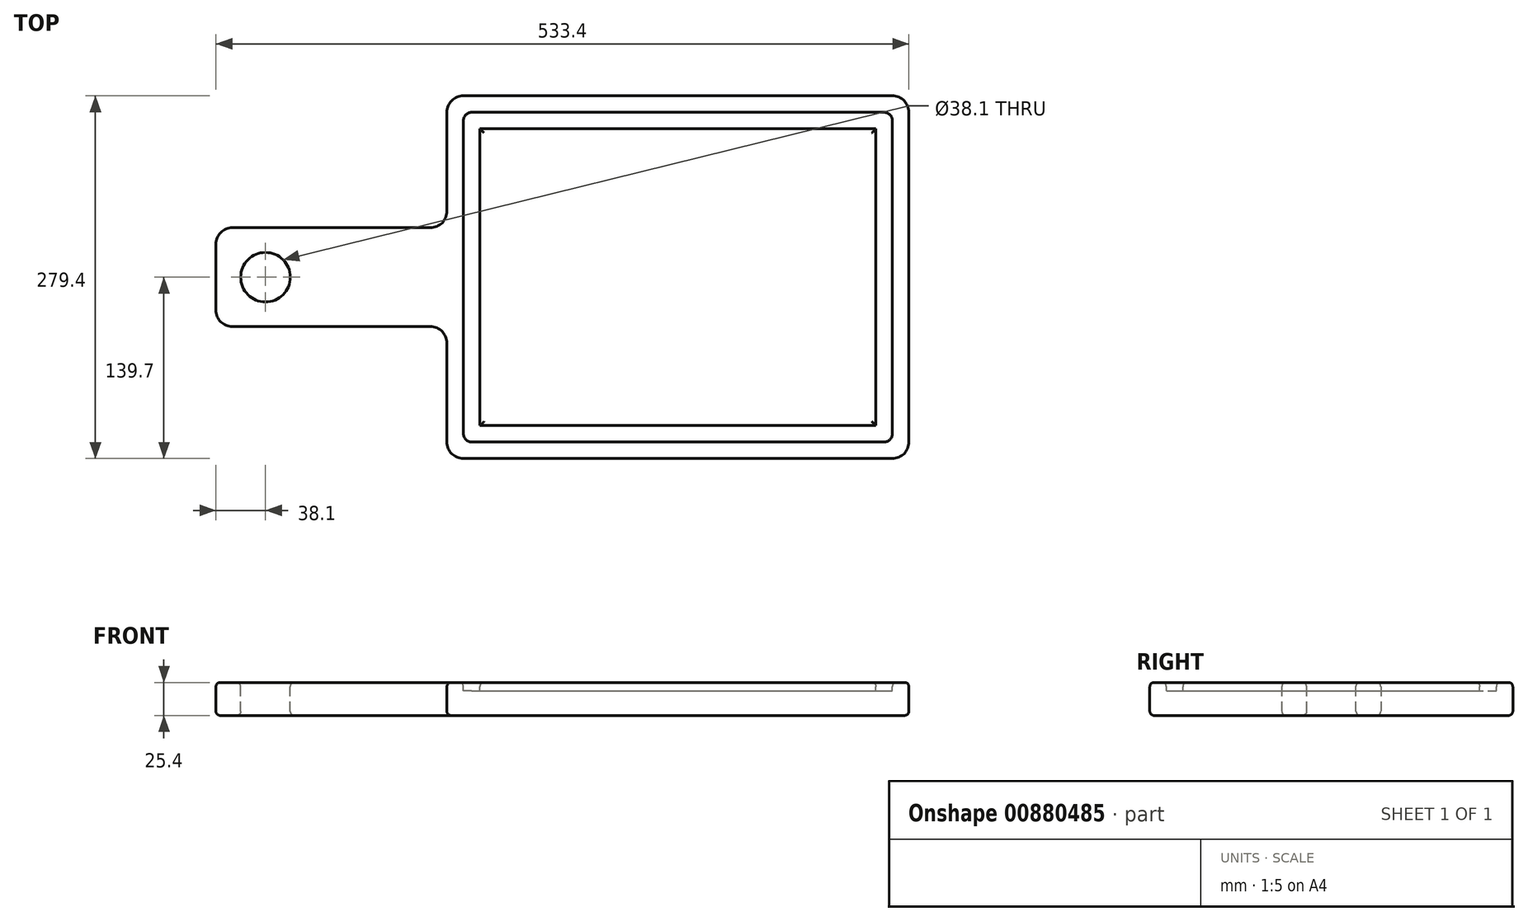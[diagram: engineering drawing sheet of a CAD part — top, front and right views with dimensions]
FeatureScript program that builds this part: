
annotation { "Feature Type Name" : "Feature", "Feature Type Description" : "" }
export const myFeature = defineFeature(function(context is Context, id is Id, definition is map)
    precondition{}
    {
        {
            var Q0;
            Q0=qCreatedBy(makeId("Top.planeOp"),FACE);
            var sketch = newSketch(context, id + "F0", { "sketchPlane" : qUnion([Q0])});
            skLineSegment(sketch, "E0.bottom", {"start": v(0, 0) * mm, "end": v(355.6, 0) * mm});
            skLineSegment(sketch, "E0.top", {"start": v(0, 279.4) * mm, "end": v(355.6, 279.4) * mm});
            skLineSegment(sketch, "E0.left", {"start": v(0, 0) * mm, "end": v(0, 279.4) * mm});
            skLineSegment(sketch, "E0.right", {"start": v(355.6, 0) * mm, "end": v(355.6, 279.4) * mm});
            skLineSegment(sketch, "E1.bottom", {"start": v(0, 177.8) * mm, "end": v(-177.8, 177.8) * mm});
            skLineSegment(sketch, "E1.top", {"start": v(0, 101.6) * mm, "end": v(-177.8, 101.6) * mm});
            skLineSegment(sketch, "E1.left", {"start": v(0, 177.8) * mm, "end": v(0, 101.6) * mm});
            skLineSegment(sketch, "E1.right", {"start": v(-177.8, 177.8) * mm, "end": v(-177.8, 101.6) * mm});
            skSolve(sketch);
        }
        {
            var Q0;
            {var subQ3=sQuery(id+"F0.wireOp",EDGE,"E0.bottom");Q0=makeQuery(id+"F0.imprint","IMPRINT",FACE,{"disambiguationData":[TD([[makeQuery(id+"F0.imprint","IMPRINT",EDGE,{"derivedFrom":subQ3}),1.0]])]});}
            var Q1;
            Q1=makeQuery(id+"F0.imprint","IMPRINT",FACE,{"disambiguationData":[TD([[makeQuery(id+"F0.imprint","IMPRINT",EDGE,{"derivedFrom":sQuery(id+"F0.wireOp",EDGE,"E1.bottom")}),1.0]])]});
            extrude(context, id + "F1", {"entities" : qUnion([Q0, Q1]), "depth" : 25.4 * mm, "offsetDistance" : 25.4 * mm});
        }
        {
            var Q0;
            Q0=makeQuery(id+"F1.opExtrude","CAP_FACE",FACE,{"disambiguationData":[OSD([sQuery(id+"F0.wireOp",EDGE,"E0.bottom"),sQuery(id+"F0.wireOp",EDGE,"E0.top"),sQuery(id+"F0.wireOp",EDGE,"E0.left"),sQuery(id+"F0.wireOp",EDGE,"E0.right"),sQuery(id+"F0.wireOp",EDGE,"E1.bottom"),sQuery(id+"F0.wireOp",EDGE,"E1.top"),sQuery(id+"F0.wireOp",EDGE,"E1.right")])],"isStart":false});
            var sketch = newSketch(context, id + "F2", { "sketchPlane" : qUnion([Q0])});
            skCircle(sketch, "E2", {"center": v(-139.7, 139.7) * mm, "radius": 19.05 * mm});
            skSolve(sketch);
        }
        {
            var Q0;
            Q0 = qSketchRegion(id + "F2", true);
            extrude(context, id + "F3", {"entities" : qUnion([Q0]), "operationType" : NewBodyOperationType.REMOVE, "oppositeDirection" : true, "depth" : 25.4 * mm, "offsetDistance" : 25.4 * mm});
        }
        {
            var Q0;
            Q0=makeQuery(id+"F1.opExtrude","CAP_FACE",FACE,{"disambiguationData":[OSD([sQuery(id+"F0.wireOp",EDGE,"E0.bottom"),sQuery(id+"F0.wireOp",EDGE,"E0.top"),sQuery(id+"F0.wireOp",EDGE,"E0.left"),sQuery(id+"F0.wireOp",EDGE,"E0.right"),sQuery(id+"F0.wireOp",EDGE,"E1.bottom"),sQuery(id+"F0.wireOp",EDGE,"E1.top"),sQuery(id+"F0.wireOp",EDGE,"E1.right")])],"isStart":false});
            var sketch = newSketch(context, id + "F4", { "sketchPlane" : qUnion([Q0])});
            skLineSegment(sketch, "E3.0", {"start": v(12.7, 12.7) * mm, "end": v(12.7, 101.6) * mm});
            skLineSegment(sketch, "E3.1", {"start": v(12.7, 177.8) * mm, "end": v(12.7, 266.7) * mm});
            skLineSegment(sketch, "E3.2", {"start": v(12.7, 266.7) * mm, "end": v(342.9, 266.7) * mm});
            skLineSegment(sketch, "E3.3", {"start": v(342.9, 12.7) * mm, "end": v(342.9, 266.7) * mm});
            skLineSegment(sketch, "E3.4", {"start": v(12.7, 12.7) * mm, "end": v(342.9, 12.7) * mm});
            skLineSegment(sketch, "E4", {"start": v(12.7, 177.8) * mm, "end": v(12.7, 101.6) * mm});
            skLineSegment(sketch, "E5.0", {"start": v(25.4, 177.8) * mm, "end": v(25.4, 254) * mm});
            skLineSegment(sketch, "E5.1", {"start": v(330.2, 25.4) * mm, "end": v(330.2, 254) * mm});
            skLineSegment(sketch, "E5.2", {"start": v(25.4, 25.4) * mm, "end": v(330.2, 25.4) * mm});
            skLineSegment(sketch, "E5.3", {"start": v(25.4, 254) * mm, "end": v(330.2, 254) * mm});
            skLineSegment(sketch, "E5.4", {"start": v(25.4, 25.4) * mm, "end": v(25.4, 101.6) * mm});
            skLineSegment(sketch, "E5.5", {"start": v(25.4, 177.8) * mm, "end": v(25.4, 101.6) * mm});
            skSolve(sketch);
        }
        {
            var Q0;
            Q0=makeQuery(id+"F4.imprint","IMPRINT",FACE,{"disambiguationData":[TD([[makeQuery(id+"F4.imprint","IMPRINT",EDGE,{"derivedFrom":sQuery(id+"F4.wireOp",EDGE,"E3.0")}),-1.0]])]});
            extrude(context, id + "F5", {"entities" : qUnion([Q0]), "operationType" : NewBodyOperationType.REMOVE, "oppositeDirection" : true, "depth" : 6.35 * mm, "offsetDistance" : 25.4 * mm});
        }
        {
            var Q0;
            Q0=makeQuery(id+"F5.boolean.opBoolean","COPY",EDGE,{"derivedFrom":makeQuery(id+"F5.opExtrude","SWEPT_EDGE",EDGE,{"disambiguationData":[OSD([sQuery(id+"F4.wireOp",EDGE,"E3.1"),sQuery(id+"F4.wireOp",EDGE,"E3.2")])]})});
            var Q1;
            Q1=makeQuery(id+"F5.boolean.opBoolean","COPY",EDGE,{"derivedFrom":makeQuery(id+"F5.opExtrude","SWEPT_EDGE",EDGE,{"disambiguationData":[OSD([sQuery(id+"F4.wireOp",EDGE,"E3.2"),sQuery(id+"F4.wireOp",EDGE,"E3.3")])]})});
            var Q2;
            Q2=makeQuery(id+"F5.boolean.opBoolean","COPY",EDGE,{"derivedFrom":makeQuery(id+"F5.opExtrude","SWEPT_EDGE",EDGE,{"disambiguationData":[OSD([sQuery(id+"F4.wireOp",EDGE,"E3.0"),sQuery(id+"F4.wireOp",EDGE,"E3.4")])]})});
            var Q3;
            Q3=makeQuery(id+"F5.boolean.opBoolean","COPY",EDGE,{"derivedFrom":makeQuery(id+"F5.opExtrude","SWEPT_EDGE",EDGE,{"disambiguationData":[OSD([sQuery(id+"F4.wireOp",EDGE,"E3.3"),sQuery(id+"F4.wireOp",EDGE,"E3.4")])]})});
            fillet(context, id + "F6", {"entities" : qUnion([Q0, Q1, Q2, Q3]), "radius" : 6.35 * mm, "tangentPropagation" : true, "allowEdgeOverflow" : false});
        }
        {
            var Q0;
            Q0=makeQuery(id+"F1.opExtrude","SWEPT_EDGE",EDGE,{"disambiguationData":[OSD([sQuery(id+"F0.wireOp",EDGE,"E0.left"),sQuery(id+"F0.wireOp",EDGE,"E1.top"),sQuery(id+"F0.wireOp",EDGE,"E1.left")])]});
            var Q1;
            Q1=makeQuery(id+"F1.opExtrude","SWEPT_EDGE",EDGE,{"disambiguationData":[OSD([sQuery(id+"F0.wireOp",EDGE,"E0.left"),sQuery(id+"F0.wireOp",EDGE,"E1.bottom"),sQuery(id+"F0.wireOp",EDGE,"E1.left")])]});
            var Q2;
            Q2=makeQuery(id+"F1.opExtrude","SWEPT_EDGE",EDGE,{"disambiguationData":[OSD([sQuery(id+"F0.wireOp",EDGE,"E0.top"),sQuery(id+"F0.wireOp",EDGE,"E0.left")])]});
            var Q3;
            Q3=makeQuery(id+"F1.opExtrude","SWEPT_EDGE",EDGE,{"disambiguationData":[OSD([sQuery(id+"F0.wireOp",EDGE,"E0.bottom"),sQuery(id+"F0.wireOp",EDGE,"E0.left")])]});
            var Q4;
            Q4=makeQuery(id+"F1.opExtrude","SWEPT_EDGE",EDGE,{"disambiguationData":[OSD([sQuery(id+"F0.wireOp",EDGE,"E1.top"),sQuery(id+"F0.wireOp",EDGE,"E1.right")])]});
            var Q5;
            Q5=makeQuery(id+"F1.opExtrude","SWEPT_EDGE",EDGE,{"disambiguationData":[OSD([sQuery(id+"F0.wireOp",EDGE,"E1.bottom"),sQuery(id+"F0.wireOp",EDGE,"E1.right")])]});
            var Q6;
            Q6=makeQuery(id+"F1.opExtrude","SWEPT_EDGE",EDGE,{"disambiguationData":[OSD([sQuery(id+"F0.wireOp",EDGE,"E0.top"),sQuery(id+"F0.wireOp",EDGE,"E0.right")])]});
            var Q7;
            Q7=makeQuery(id+"F1.opExtrude","SWEPT_EDGE",EDGE,{"disambiguationData":[OSD([sQuery(id+"F0.wireOp",EDGE,"E0.bottom"),sQuery(id+"F0.wireOp",EDGE,"E0.right")])]});
            fillet(context, id + "F7", {"entities" : qUnion([Q0, Q1, Q2, Q3, Q4, Q5, Q6, Q7]), "radius" : 12.7 * mm, "tangentPropagation" : true, "allowEdgeOverflow" : false});
        }
        {
            var Q0;
            Q0=makeQuery(id+"F5.boolean.opBoolean","SPLIT",FACE,{"disambiguationData":[TD([makeQuery(id+"F5.opExtrude","SWEPT_FACE",FACE,{"disambiguationData":[OSD([sQuery(id+"F4.wireOp",EDGE,"E5.1")])]})])],"derivedFrom":makeQuery(id+"F1.opExtrude","CAP_FACE",FACE,{"disambiguationData":[OSD([sQuery(id+"F0.wireOp",EDGE,"E0.bottom"),sQuery(id+"F0.wireOp",EDGE,"E0.top"),sQuery(id+"F0.wireOp",EDGE,"E0.left"),sQuery(id+"F0.wireOp",EDGE,"E0.right"),sQuery(id+"F0.wireOp",EDGE,"E1.bottom"),sQuery(id+"F0.wireOp",EDGE,"E1.top"),sQuery(id+"F0.wireOp",EDGE,"E1.right")])],"isStart":false})});
            var Q1;
            {var subQ0=sQuery(id+"F0.wireOp",EDGE,"E1.right");var subQ1=sQuery(id+"F0.wireOp",EDGE,"E1.top");var subQ2=sQuery(id+"F0.wireOp",EDGE,"E1.bottom");var subQ3=sQuery(id+"F0.wireOp",EDGE,"E0.right");var subQ4=sQuery(id+"F0.wireOp",EDGE,"E0.bottom");var subQ5=sQuery(id+"F0.wireOp",EDGE,"E0.left");var subQ6=sQuery(id+"F0.wireOp",EDGE,"E0.top");Q1=makeQuery(id+"F5.boolean.opBoolean","SPLIT",FACE,{"disambiguationData":[TD([makeQuery(id+"F1.opExtrude","SWEPT_FACE",FACE,{"disambiguationData":[OSD([subQ4])]})])],"derivedFrom":makeQuery(id+"F1.opExtrude","CAP_FACE",FACE,{"disambiguationData":[OSD([subQ4,subQ6,subQ5,subQ3,subQ2,subQ1,subQ0])],"isStart":false})});}
            var Q2;
            Q2=makeQuery(id+"F1.opExtrude","CAP_FACE",FACE,{"disambiguationData":[OSD([sQuery(id+"F0.wireOp",EDGE,"E0.bottom"),sQuery(id+"F0.wireOp",EDGE,"E0.top"),sQuery(id+"F0.wireOp",EDGE,"E0.left"),sQuery(id+"F0.wireOp",EDGE,"E0.right"),sQuery(id+"F0.wireOp",EDGE,"E1.bottom"),sQuery(id+"F0.wireOp",EDGE,"E1.top"),sQuery(id+"F0.wireOp",EDGE,"E1.right")])],"isStart":true});
            fillet(context, id + "F8", {"entities" : qUnion([Q0, Q1, Q2]), "radius" : 3.17 * mm, "tangentPropagation" : true, "allowEdgeOverflow" : false});
        }
    });
